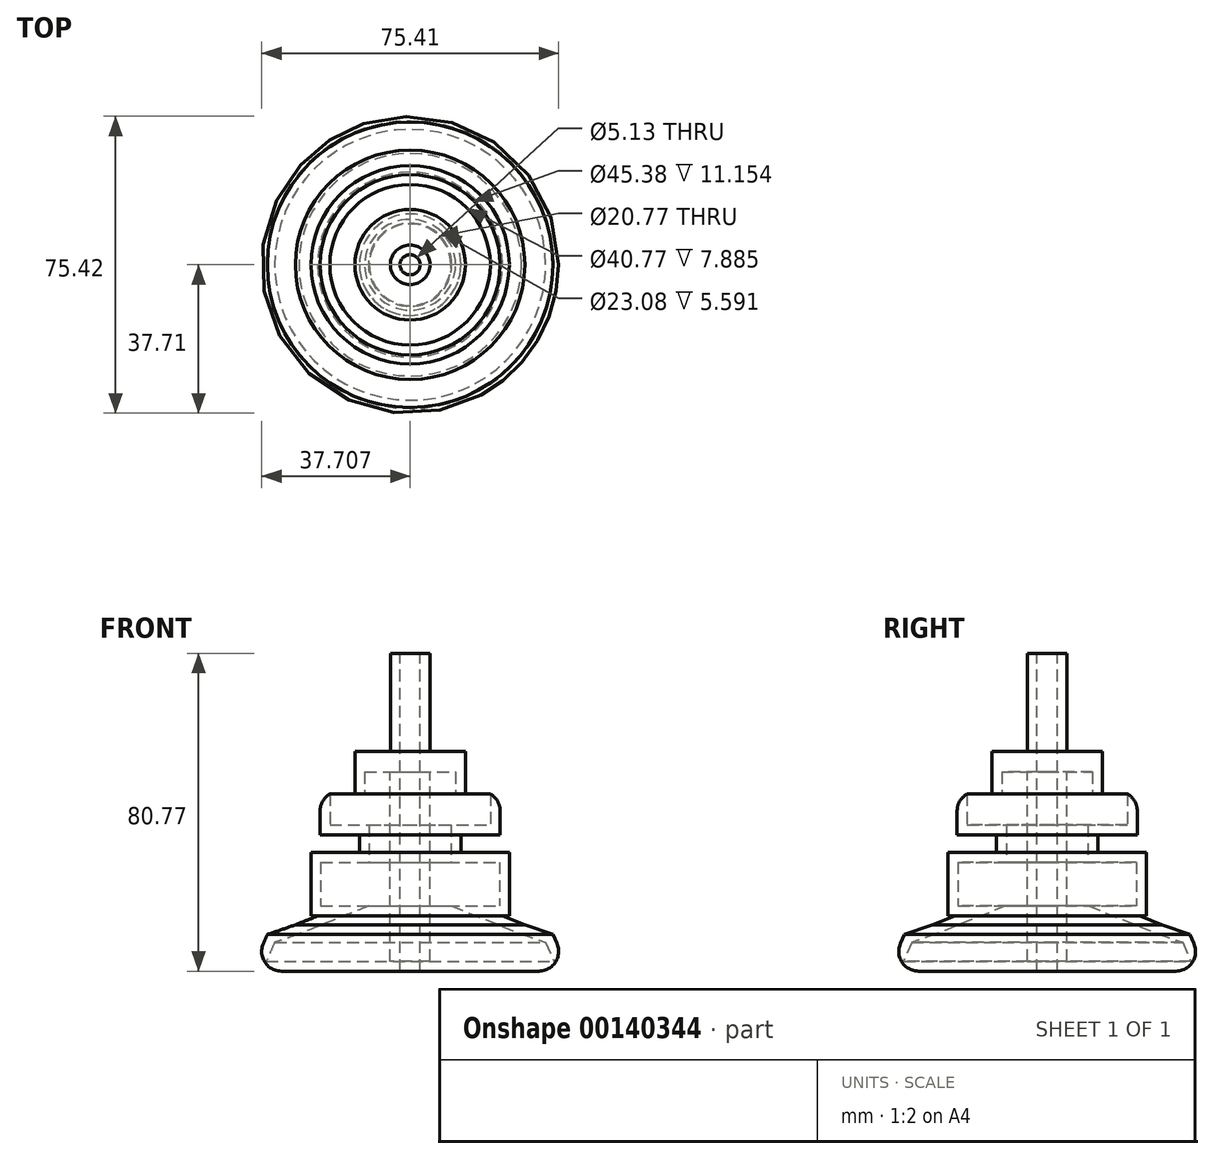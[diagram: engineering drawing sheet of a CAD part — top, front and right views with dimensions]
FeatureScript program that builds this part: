
annotation { "Feature Type Name" : "Feature", "Feature Type Description" : "" }
export const myFeature = defineFeature(function(context is Context, id is Id, definition is map)
    precondition{}
    {
        {
            var Q0;
            Q0=qCreatedBy(makeId("Front.planeOp"),FACE);
            var sketch = newSketch(context, id + "F0", { "sketchPlane" : qUnion([Q0])});
            skLineSegment(sketch, "E0", {"start": v(28.08, 50.77) * mm, "end": v(39.62, 50.77) * mm});
            skLineSegment(sketch, "E1", {"start": v(39.62, 50.77) * mm, "end": v(39.62, 42.5) * mm});
            skLineSegment(sketch, "E2", {"start": v(39.62, 42.5) * mm, "end": v(48.46, 42.5) * mm});
            skLineSegment(sketch, "E3", {"start": v(48.46, 42.5) * mm, "end": v(48.46, 34.62) * mm});
            skLineSegment(sketch, "E4", {"start": v(48.46, 34.62) * mm, "end": v(38.46, 34.62) * mm});
            skLineSegment(sketch, "E5", {"start": v(38.46, 34.62) * mm, "end": v(38.46, 25.2) * mm});
            skLineSegment(sketch, "E6", {"start": v(38.46, 25.2) * mm, "end": v(50.77, 25.2) * mm});
            skLineSegment(sketch, "E7", {"start": v(50.77, 25.2) * mm, "end": v(50.77, 14.04) * mm});
            skLineSegment(sketch, "E8", {"start": v(50.77, 14.04) * mm, "end": v(38.65, 14.04) * mm});
            skLineSegment(sketch, "E9", {"start": v(38.65, 14.04) * mm, "end": v(56.35, 6.92) * mm});
            skLineSegment(sketch, "E10", {"start": v(56.35, 6.92) * mm, "end": v(62.5, 4.8) * mm});
            skLineSegment(sketch, "E11", {"start": v(62.5, 4.8) * mm, "end": v(64.62, 0) * mm});
            skLineSegment(sketch, "E12", {"start": v(64.62, 0) * mm, "end": v(28.08, 0) * mm});
            skLineSegment(sketch, "E13", {"start": v(28.08, 0) * mm, "end": v(28.08, 50.77) * mm});
            skSolve(sketch);
        }
        {
            var Q0;
            Q0=makeQuery(id+"F0.imprint","IMPRINT",FACE,{"disambiguationData":[TD([[makeQuery(id+"F0.imprint","IMPRINT",EDGE,{"derivedFrom":sQuery(id+"F0.wireOp",EDGE,"E0")}),-1.0]])]});
            var Q1;
            Q1=sQuery(id+"F0.wireOp",EDGE,"E13");
            revolve(context, id + "F1", {"entities" : qUnion([Q0]), "axis" : qUnion([Q1]), "revolveType" : RevolveType.FULL});
        }
        {
            var Q0;
            Q0=makeQuery(id+"F1.opRevolve","SWEPT_FACE",FACE,{"disambiguationData":[OSD([sQuery(id+"F0.wireOp",EDGE,"E0")])]});
            var sketch = newSketch(context, id + "F2", { "sketchPlane" : qUnion([Q0])});
            skCircle(sketch, "E14", {"center": v(28.08, 0) * mm, "radius": 5.06 * mm});
            skSolve(sketch);
        }
        {
            var Q0;
            Q0=makeQuery(id+"F2.imprint","IMPRINT",FACE,{"disambiguationData":[TD([[makeQuery(id+"F2.imprint","IMPRINT",EDGE,{"derivedFrom":sQuery(id+"F2.wireOp",EDGE,"E14")}),1.0]])]});
            extrude(context, id + "F3", {"entities" : qUnion([Q0]), "operationType" : NewBodyOperationType.REMOVE, "endBound" : BoundingType.THROUGH_ALL, "oppositeDirection" : true, "depth" : 25 * mm});
        }
        {
            var Q0;
            Q0=makeQuery(id+"F1.opRevolve","SWEPT_FACE",FACE,{"disambiguationData":[OSD([sQuery(id+"F0.wireOp",EDGE,"E2")])]});
            shell(context, id + "F4", {"entities" : qUnion([Q0]), "thickness" : 2.5 * mm, "oppositeDirection" : true});
        }
        {
            var Q0;
            Q0=makeQuery(id+"F1.opRevolve","SWEPT_EDGE",EDGE,{"disambiguationData":[OSD([sQuery(id+"F0.wireOp",EDGE,"E2"),sQuery(id+"F0.wireOp",EDGE,"E3")])]});
            fillet(context, id + "F5", {"entities" : qUnion([Q0]), "radius" : 5 * mm, "tangentPropagation" : true, "allowEdgeOverflow" : false});
        }
        {
            var Q0;
            Q0=makeQuery(id+"F1.opRevolve","SWEPT_EDGE",EDGE,{"disambiguationData":[OSD([sQuery(id+"F0.wireOp",EDGE,"E11"),sQuery(id+"F0.wireOp",EDGE,"E12")])]});
            fillet(context, id + "F6", {"entities" : qUnion([Q0]), "radius" : 5 * mm, "tangentPropagation" : true, "allowEdgeOverflow" : false});
        }
        {
            var Q0;
            Q0=makeQuery(id+"F1.opRevolve","SWEPT_FACE",FACE,{"disambiguationData":[OSD([sQuery(id+"F0.wireOp",EDGE,"E0")])]});
            var sketch = newSketch(context, id + "F7", { "sketchPlane" : qUnion([Q0])});
            skCircle(sketch, "E15.0", {"center": v(28.08, 0) * mm, "radius": 5.03 * mm});
            skSolve(sketch);
        }
        {
            var Q0;
            Q0=makeQuery(id+"F7.imprint","IMPRINT",FACE,{"disambiguationData":[TD([[makeQuery(id+"F7.imprint","IMPRINT",EDGE,{"derivedFrom":sQuery(id+"F7.wireOp",EDGE,"E15.0")}),1.0]])]});
            extrude(context, id + "F8", {"entities" : qUnion([Q0]), "operationType" : NewBodyOperationType.ADD, "depth" : 25 * mm});
        }
        {
            var Q0;
            Q0=makeQuery(id+"F1.opRevolve","SWEPT_FACE",FACE,{"disambiguationData":[OSD([sQuery(id+"F0.wireOp",EDGE,"E0")])]});
            extrude(context, id + "F9", {"entities" : qUnion([Q0]), "operationType" : NewBodyOperationType.ADD, "oppositeDirection" : true, "depth" : 5.18 * mm});
        }
    });
